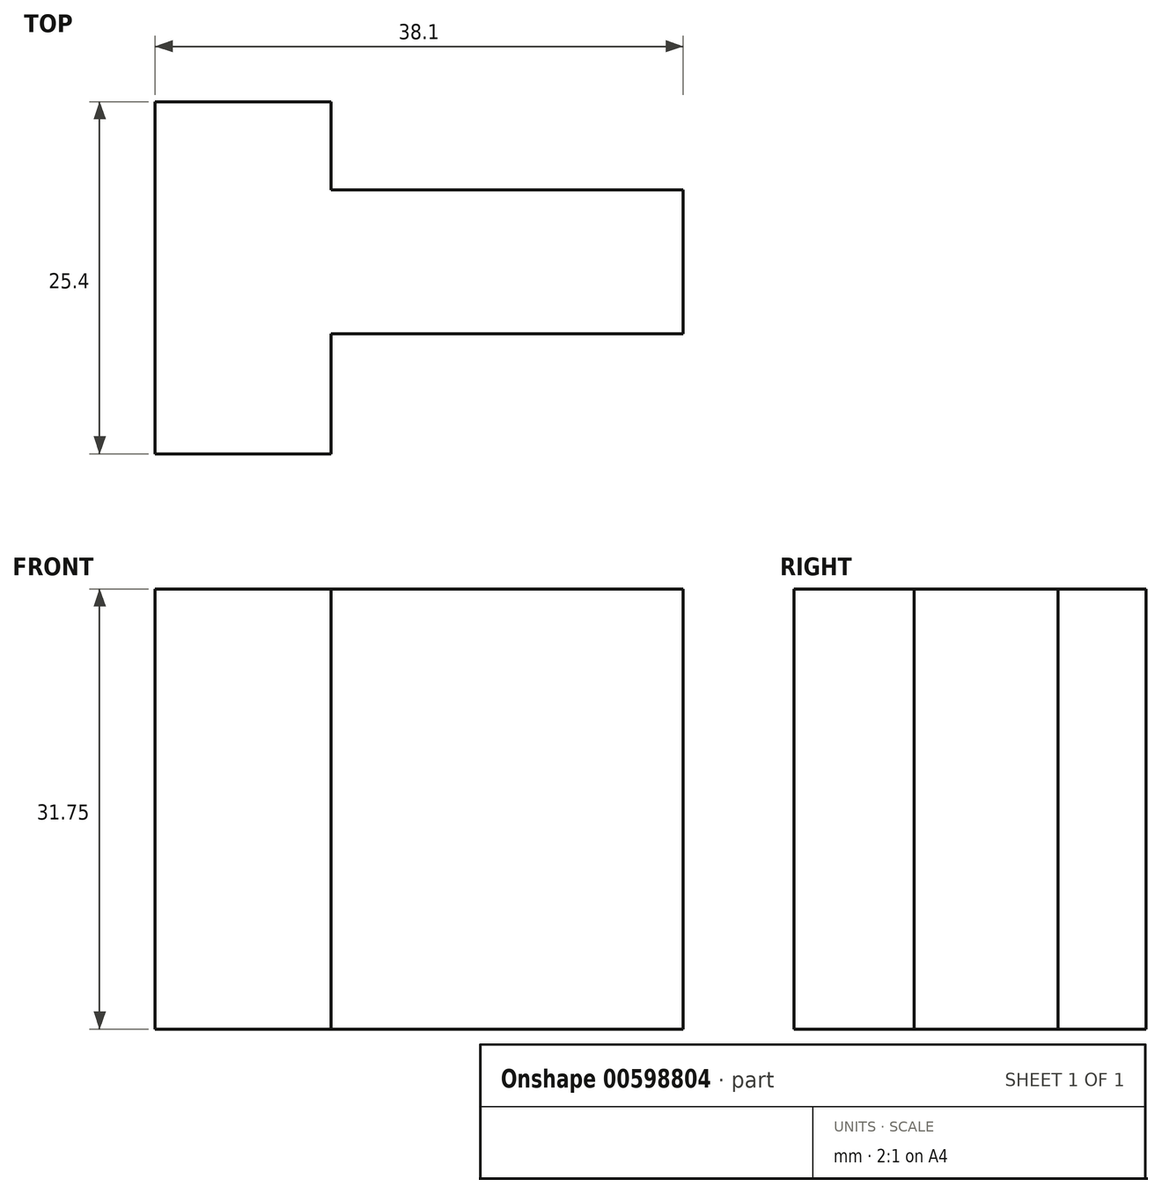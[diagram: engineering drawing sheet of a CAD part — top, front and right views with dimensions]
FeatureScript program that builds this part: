
annotation { "Feature Type Name" : "Feature", "Feature Type Description" : "" }
export const myFeature = defineFeature(function(context is Context, id is Id, definition is map)
    precondition{}
    {
        {
            var Q0;
            Q0=qCreatedBy(makeId("Top.planeOp"),FACE);
            var sketch = newSketch(context, id + "F0", { "sketchPlane" : qUnion([Q0])});
            skLineSegment(sketch, "E0", {"start": v(0, 0) * mm, "end": v(0, 25.4) * mm});
            skLineSegment(sketch, "E1", {"start": v(0, 25.4) * mm, "end": v(12.7, 25.4) * mm});
            skLineSegment(sketch, "E2", {"start": v(12.7, 25.4) * mm, "end": v(12.7, 19.05) * mm});
            skLineSegment(sketch, "E3", {"start": v(12.7, 19.05) * mm, "end": v(38.1, 19.05) * mm});
            skLineSegment(sketch, "E4", {"start": v(38.1, 19.05) * mm, "end": v(38.1, 8.66) * mm});
            skLineSegment(sketch, "E5", {"start": v(38.1, 8.66) * mm, "end": v(12.7, 8.66) * mm});
            skPoint(sketch, "E5.endSnap0", {"position": v(12.7, 22.23) * mm});
            skLineSegment(sketch, "E6", {"start": v(12.7, 8.66) * mm, "end": v(12.7, 0) * mm});
            skLineSegment(sketch, "E7", {"start": v(12.7, 0) * mm, "end": v(0, 0) * mm});
            skSolve(sketch);
        }
        {
            var Q0;
            Q0 = qSketchRegion(id + "F0", true);
            extrude(context, id + "F1", {"entities" : qUnion([Q0]), "depth" : 31.75 * mm, "offsetDistance" : 25.4 * mm});
        }
    });
